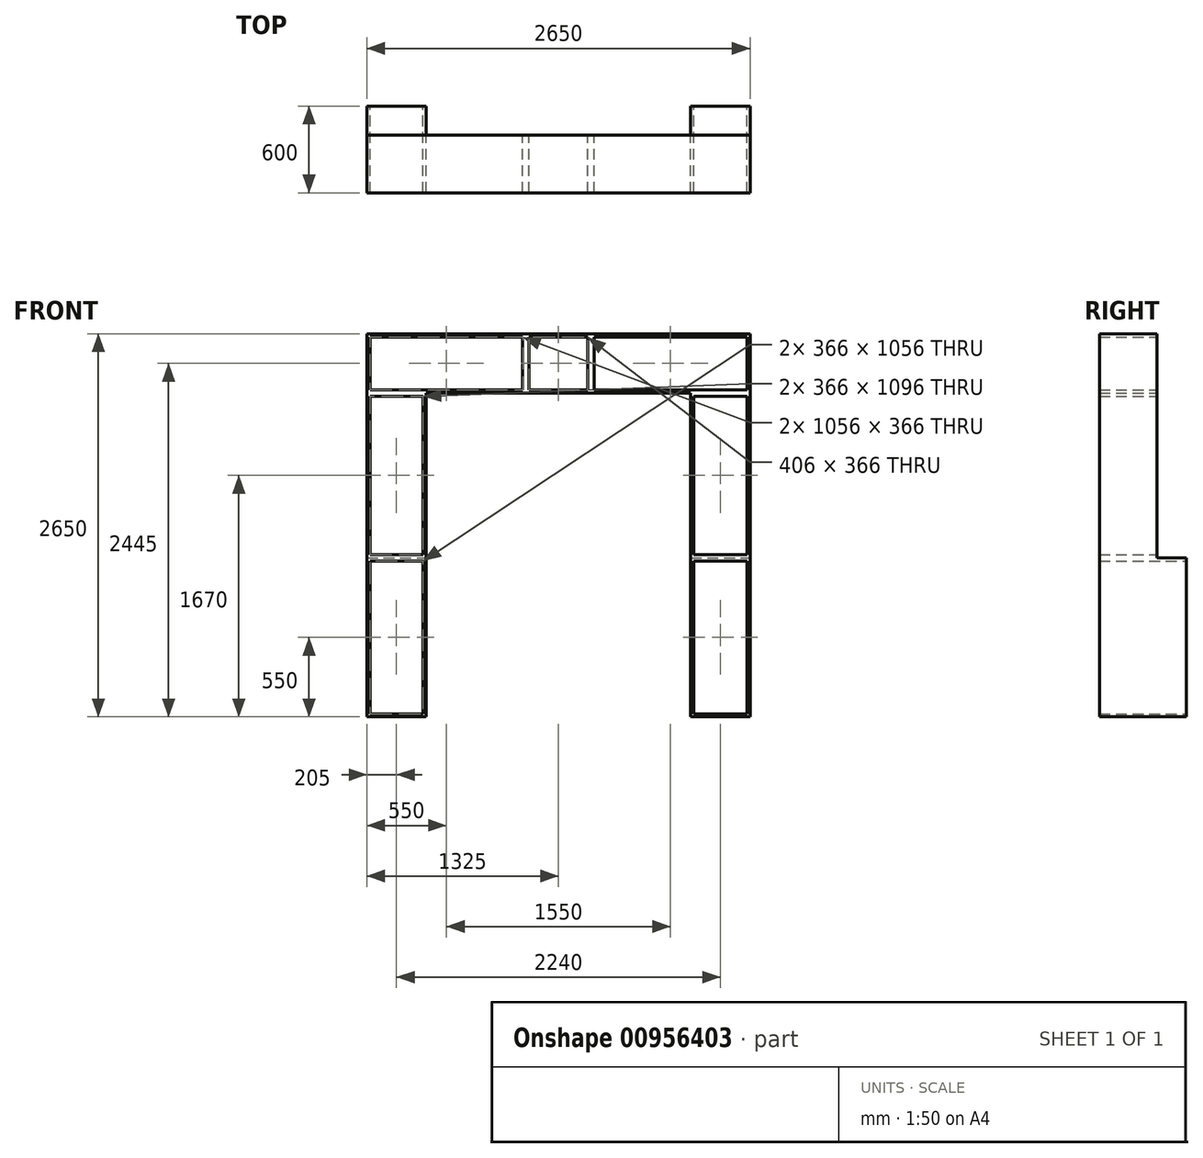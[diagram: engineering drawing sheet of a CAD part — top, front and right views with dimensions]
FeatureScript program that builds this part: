
annotation { "Feature Type Name" : "Feature", "Feature Type Description" : "" }
export const myFeature = defineFeature(function(context is Context, id is Id, definition is map)
    precondition{}
    {
        {
            var Q0;
            Q0=qCreatedBy(makeId("Front.planeOp"),FACE);
            var sketch = newSketch(context, id + "F0", { "sketchPlane" : qUnion([Q0])});
            skLineSegment(sketch, "E0.bottom", {"start": v(-1325, 1325) * mm, "end": v(1325, 1325) * mm});
            skLineSegment(sketch, "E0.top", {"start": v(-1325, -1325) * mm, "end": v(-915, -1325) * mm});
            skLineSegment(sketch, "E0.left", {"start": v(-1325, 1325) * mm, "end": v(-1325, -1325) * mm});
            skLineSegment(sketch, "E0.right", {"start": v(1325, 1325) * mm, "end": v(1325, -203) * mm});
            skPoint(sketch, "E0.middle", {"position": v(0, 0) * mm});
            skLineSegment(sketch, "E1.left", {"start": v(915, -1325) * mm, "end": v(915, -203) * mm});
            skLineSegment(sketch, "E1.right", {"start": v(-915, -1325) * mm, "end": v(-915, 915) * mm});
            skLineSegment(sketch, "E2.trimOffspring", {"start": v(915, -1325) * mm, "end": v(1325, -1325) * mm});
            skLineSegment(sketch, "E3.0", {"start": v(-1303, 1303) * mm, "end": v(-247, 1303) * mm});
            skLineSegment(sketch, "E3.1", {"start": v(1303, 1303) * mm, "end": v(1303, 937) * mm});
            skLineSegment(sketch, "E3.2", {"start": v(-1303, 1303) * mm, "end": v(-1303, 937) * mm});
            skLineSegment(sketch, "E3.3", {"start": v(937, -1303) * mm, "end": v(1303, -1303) * mm});
            skLineSegment(sketch, "E3.4", {"start": v(-1303, -1303) * mm, "end": v(-937, -1303) * mm});
            skLineSegment(sketch, "E3.5", {"start": v(-937, -1303) * mm, "end": v(-937, -247) * mm});
            skLineSegment(sketch, "E3.6", {"start": v(1303, 937) * mm, "end": v(247, 937) * mm});
            skLineSegment(sketch, "E3.7", {"start": v(937, -1303) * mm, "end": v(937, -247) * mm});
            skLineSegment(sketch, "E4.left", {"start": v(-247, 1303) * mm, "end": v(-247, 937) * mm});
            skLineSegment(sketch, "E5.left", {"start": v(247, 1303) * mm, "end": v(247, 937) * mm});
            skLineSegment(sketch, "E6", {"start": v(-203, 1303) * mm, "end": v(-203, 937) * mm});
            skLineSegment(sketch, "E7", {"start": v(203, 1303) * mm, "end": v(203, 937) * mm});
            skLineSegment(sketch, "E8", {"start": v(-1303, 893) * mm, "end": v(-937, 893) * mm});
            skLineSegment(sketch, "E9", {"start": v(1303, 893) * mm, "end": v(937, 893) * mm});
            skLineSegment(sketch, "E10.0", {"start": v(-1303, -247) * mm, "end": v(-937, -247) * mm});
            skLineSegment(sketch, "E11.0", {"start": v(-1303, -203) * mm, "end": v(-937, -203) * mm});
            skLineSegment(sketch, "E12.MirrorCS", {"start": v(1303, -203) * mm, "end": v(937, -203) * mm});
            skLineSegment(sketch, "E13.MirrorCS", {"start": v(1303, -247) * mm, "end": v(937, -247) * mm});
            skPoint(sketch, "E14.orphan", {"position": v(-1325, -203) * mm});
            skPoint(sketch, "E15.orphan", {"position": v(-1325, -247) * mm});
            skPoint(sketch, "E16.orphan", {"position": v(-915, -203) * mm});
            skPoint(sketch, "E17.orphan", {"position": v(-915, -247) * mm});
            skLineSegment(sketch, "E18.trimOffspring", {"start": v(-1303, -247) * mm, "end": v(-1303, -1303) * mm});
            skLineSegment(sketch, "E19.trimOffspring", {"start": v(-937, -203) * mm, "end": v(-937, 893) * mm});
            skLineSegment(sketch, "E20.trimOffspring", {"start": v(-1303, 893) * mm, "end": v(-1303, -203) * mm});
            skLineSegment(sketch, "E21", {"start": v(-915, 915) * mm, "end": v(915, 915) * mm});
            skLineSegment(sketch, "E22.trimOffspring", {"start": v(1303, 893) * mm, "end": v(1303, -203) * mm});
            skLineSegment(sketch, "E23.trimOffspring", {"start": v(-247, 937) * mm, "end": v(-1303, 937) * mm});
            skLineSegment(sketch, "E24.trimOffspring", {"start": v(203, 937) * mm, "end": v(-203, 937) * mm});
            skLineSegment(sketch, "E25.trimOffspring", {"start": v(247, 1303) * mm, "end": v(1303, 1303) * mm});
            skLineSegment(sketch, "E26.trimOffspring", {"start": v(-203, 1303) * mm, "end": v(203, 1303) * mm});
            skPoint(sketch, "E27.orphan", {"position": v(915, -203) * mm});
            skPoint(sketch, "E28.orphan", {"position": v(915, -247) * mm});
            skLineSegment(sketch, "E29.trimOffspring", {"start": v(937, -203) * mm, "end": v(937, 893) * mm});
            skLineSegment(sketch, "E30.trimOffspring", {"start": v(1303, -247) * mm, "end": v(1303, -1303) * mm});
            skPoint(sketch, "E31.orphan", {"position": v(1325, -203) * mm});
            skPoint(sketch, "E32.orphan", {"position": v(1325, -247) * mm});
            skLineSegment(sketch, "E33.trimOffspring", {"start": v(1325, -203) * mm, "end": v(1325, -1325) * mm});
            skLineSegment(sketch, "E34.trimOffspring", {"start": v(915, -203) * mm, "end": v(915, 915) * mm});
            skSolve(sketch);
        }
        {
            var Q0;
            Q0=makeQuery(id+"F0.imprint","IMPRINT",FACE,{"disambiguationData":[TD([[makeQuery(id+"F0.imprint","IMPRINT",EDGE,{"derivedFrom":sQuery(id+"F0.wireOp",EDGE,"E0.bottom")}),-1.0]])]});
            extrude(context, id + "F1", {"entities" : qUnion([Q0]), "depth" : 600 * mm, "offsetDistance" : 25 * mm});
        }
        {
            var Q0;
            Q0=makeQuery(id+"F1.opExtrude","SWEPT_FACE",FACE,{"disambiguationData":[OSD([sQuery(id+"F0.wireOp",EDGE,"E0.right"),sQuery(id+"F0.wireOp",EDGE,"E33.trimOffspring")])]});
            var sketch = newSketch(context, id + "F2", { "sketchPlane" : qUnion([Q0])});
            skLineSegment(sketch, "E35.bottom", {"start": v(0, 1325) * mm, "end": v(-200, 1325) * mm});
            skLineSegment(sketch, "E35.top", {"start": v(0, -225) * mm, "end": v(-200, -225) * mm});
            skLineSegment(sketch, "E35.left", {"start": v(0, 1325) * mm, "end": v(0, -225) * mm});
            skLineSegment(sketch, "E35.right", {"start": v(-200, 1325) * mm, "end": v(-200, -225) * mm});
            skSolve(sketch);
        }
        {
            var Q0;
            Q0=makeQuery(id+"F2.imprint","IMPRINT",FACE,{"disambiguationData":[TD([[makeQuery(id+"F2.imprint","IMPRINT",EDGE,{"derivedFrom":sQuery(id+"F2.wireOp",EDGE,"E35.bottom")}),-1.0]])]});
            extrude(context, id + "F3", {"entities" : qUnion([Q0]), "operationType" : NewBodyOperationType.REMOVE, "endBound" : BoundingType.THROUGH_ALL, "oppositeDirection" : true, "depth" : 3670 * mm, "offsetDistance" : 25 * mm});
        }
    });
